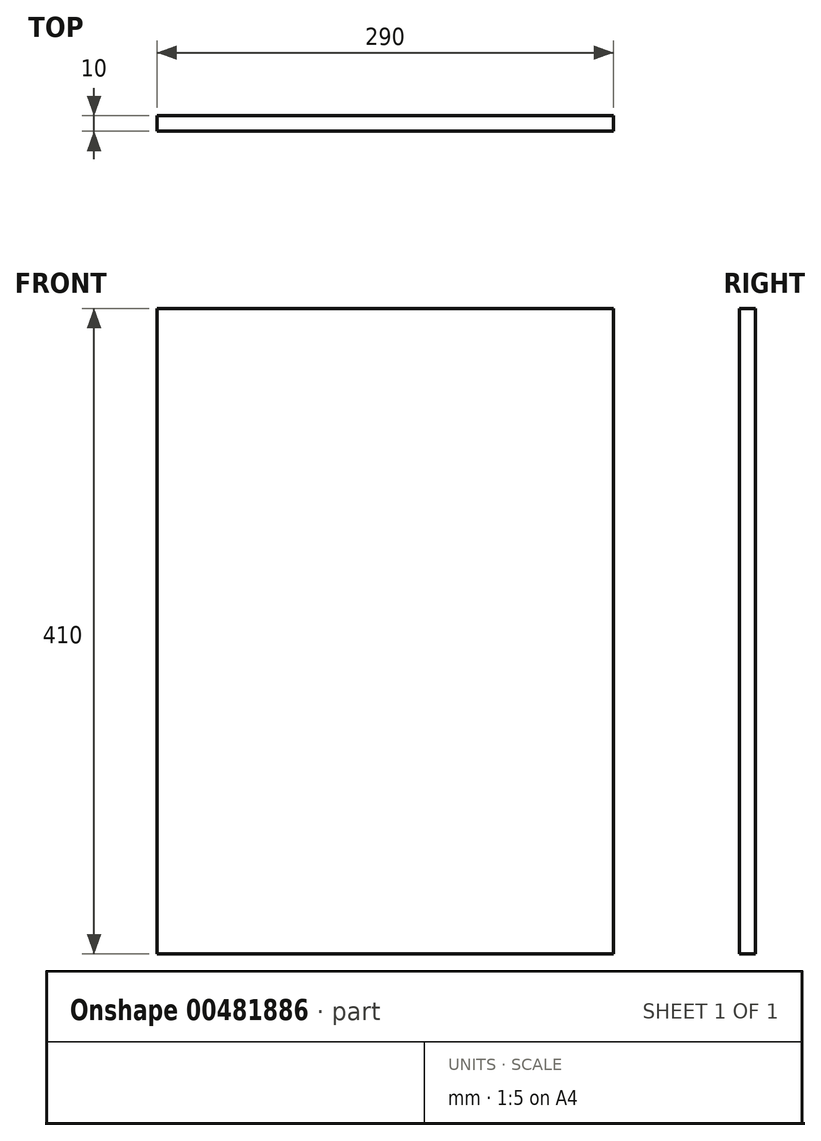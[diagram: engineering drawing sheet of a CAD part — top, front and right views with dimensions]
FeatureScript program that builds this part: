
annotation { "Feature Type Name" : "Feature", "Feature Type Description" : "" }
export const myFeature = defineFeature(function(context is Context, id is Id, definition is map)
    precondition{}
    {
        {
            var Q0;
            Q0=qCreatedBy(makeId("Front.planeOp"),FACE);
            var sketch = newSketch(context, id + "F0", { "sketchPlane" : qUnion([Q0])});
            skLineSegment(sketch, "E0.bottom", {"start": v(0, 0) * mm, "end": v(-290, 0) * mm});
            skLineSegment(sketch, "E0.top", {"start": v(0, 410) * mm, "end": v(-290, 410) * mm});
            skLineSegment(sketch, "E0.left", {"start": v(0, 0) * mm, "end": v(0, 410) * mm});
            skLineSegment(sketch, "E0.right", {"start": v(-290, 0) * mm, "end": v(-290, 410) * mm});
            skSolve(sketch);
        }
        {
            var Q0;
            Q0 = qSketchRegion(id + "F0", true);
            extrude(context, id + "F1", {"entities" : qUnion([Q0]), "depth" : 10 * mm});
        }
    });
